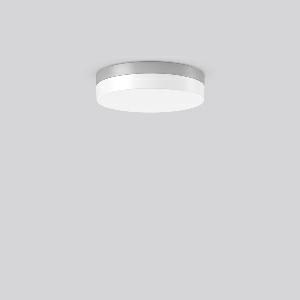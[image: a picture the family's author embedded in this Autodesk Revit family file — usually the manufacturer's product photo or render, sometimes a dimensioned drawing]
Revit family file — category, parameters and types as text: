
# Revit family: flat_slim_round_312630_004_19_2d02
name_source: partatom
category: Lighting Fixtures
units: mm (PartAtom-declared; Revit-internal decimal feet)

## family parameters
Cut with Voids When Loaded = No
Host = Face
Light Source = No
Part Type = Normal
Room Calculation Point = No
Round Connector Dimension = Use Diameter
Shared = No

## types (1)
- MultiLumen 1 830 (1 x LED Modul 830, 1300 lm, 3000)
    Apparent Load = 11 VA
    CIE Flux Codes = 39 70 89 83 100
    Color Rendering = 80
    Color Temperature = 3000
    Default Elevation = 1800 mm
    Height = 70 mm
    Lamp = 1 x LED Modul 830
    Lamp Light Flux = 1300 lm
    Lamp count = 1
    Length = 300 mm
    Lifetime = 50000 h
    Luminous efficacy = 118 lm/W
    Manufacturer = RZB
    ModVariant = No
    Model = 312630.004.19
    Mounting Place = Ceiling
    Mounting Type = Surface mounted
    Number of Poles = 1
    OnlyDefault = Yes
    Power Factor = 1
    Product Name = FLAT SLIM round
    Product group = Surface mounted ceiling and wall luminaires
    ProductGroupID = 305
    Protection Class = Protection class I
    Protection Degree = Degree of protection
    RLX_Detail_Level = 1
    RLX_Emergency_Light_Flux = 0 lm
    RLX_Emergency_Type = 0
    RLX_Emergency_Type_DB = No
    RlxData = <blob elided: 17341 chars, md5=0d80c300>
    Socket = socket
    Standby Power = 0 W
    System Light Flux = 1300 lm
    System Power = 11 W
    Type Comments = MultiLumen 1 830
    Type Image = 312629.004.jpg
    URL = http://relux.com
    VarID = multilumen_1_830
    Voltage = 0 V
    Weight = 0.00 kg
    Width = 0 mm  [stored 0 ft]

note: [stored X ft] marks values corroborated as IEEE doubles in the binary element streams (Revit-internal decimal feet)

## geometry (parser evidence)
native form markers: Blend x4, Sweep x14
no freeform markers — native parametric forms only
